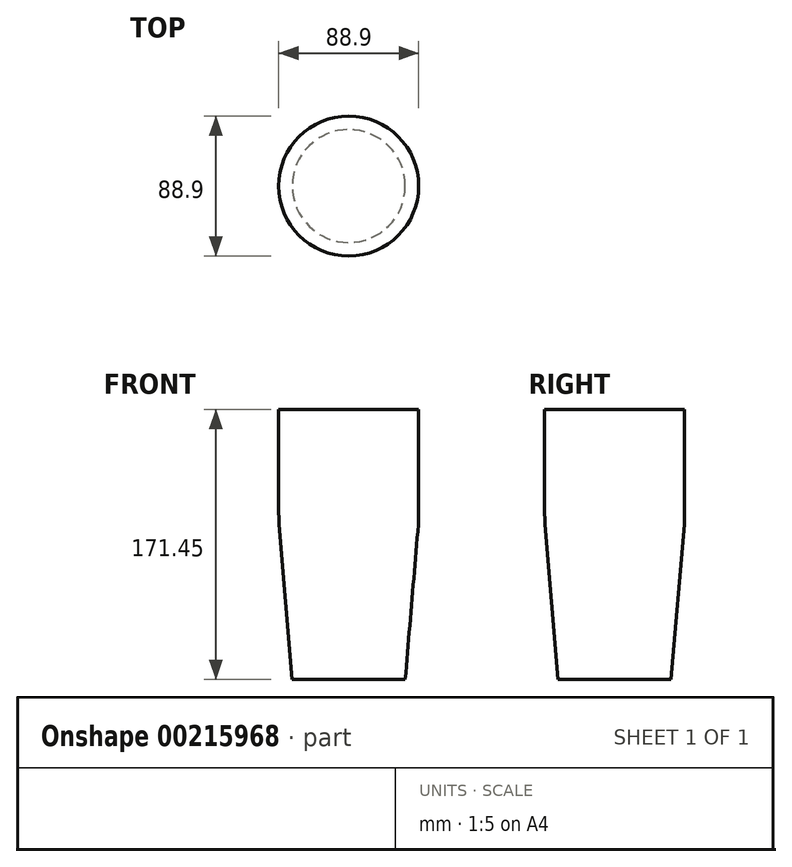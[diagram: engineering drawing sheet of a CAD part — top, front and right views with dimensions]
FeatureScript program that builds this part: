
annotation { "Feature Type Name" : "Feature", "Feature Type Description" : "" }
export const myFeature = defineFeature(function(context is Context, id is Id, definition is map)
    precondition{}
    {
        {
            var Q0;
            Q0=qCreatedBy(makeId("Front.planeOp"),FACE);
            var sketch = newSketch(context, id + "F0", { "sketchPlane" : qUnion([Q0])});
            skLineSegment(sketch, "E0", {"start": v(0, 0) * mm, "end": v(35.88, 0) * mm});
            skLineSegment(sketch, "E1", {"start": v(35.88, 0) * mm, "end": v(44.18, 98.4) * mm});
            skLineSegment(sketch, "E2", {"start": v(44.45, 104.8) * mm, "end": v(44.45, 171.45) * mm});
            skLineSegment(sketch, "E3", {"start": v(44.45, 171.45) * mm, "end": v(0, 171.45) * mm});
            skLineSegment(sketch, "E4", {"start": v(0, 171.45) * mm, "end": v(0, 0) * mm});
            skPoint(sketch, "E5.visualSharp", {"position": v(44.45, 101.6) * mm});
            skArc(sketch, "E5.filletArc", {"start": v(44.18, 98.4) * mm, "mid": v(44.38, 101.6) * mm, "end": v(44.45, 104.8) * mm});
            skSolve(sketch);
        }
        {
            var Q0;
            Q0=qSketchRegion(id+"F0",true);
            var Q1;
            Q1=sQuery(id+"F0.wireOp",EDGE,"E4");
            revolve(context, id + "F1", {"entities" : qUnion([Q0]), "axis" : qUnion([Q1]), "revolveType" : RevolveType.FULL});
        }
    });
